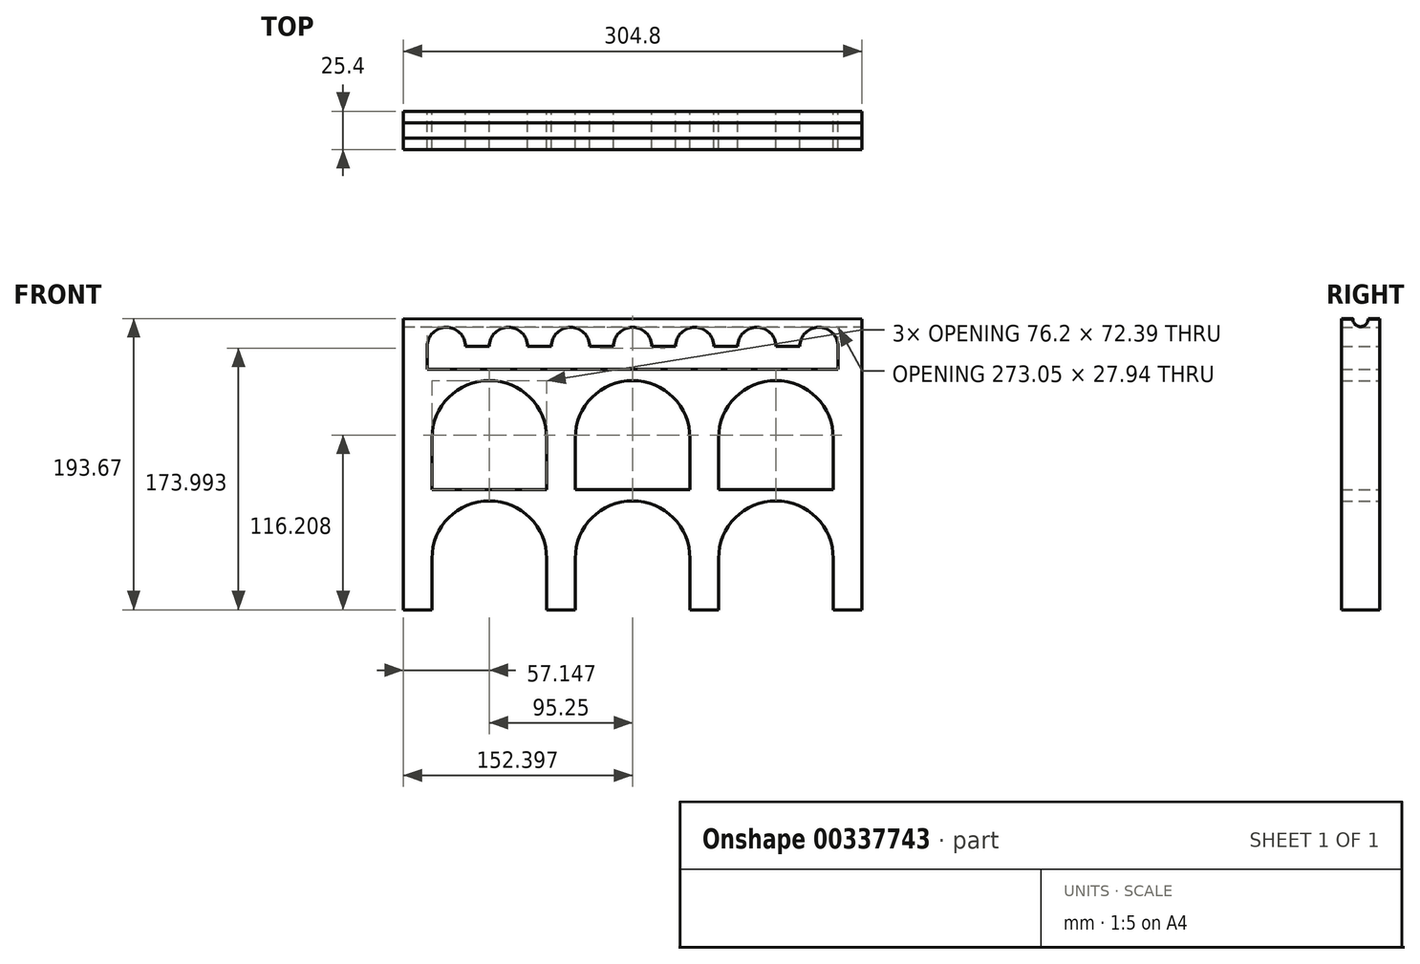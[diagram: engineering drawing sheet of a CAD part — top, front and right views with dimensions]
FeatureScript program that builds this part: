
annotation { "Feature Type Name" : "Feature", "Feature Type Description" : "" }
export const myFeature = defineFeature(function(context is Context, id is Id, definition is map)
    precondition{}
    {
        {
            var Q0;
            Q0=qCreatedBy(makeId("Front.planeOp"),FACE);
            var sketch = newSketch(context, id + "F0", { "sketchPlane" : qUnion([Q0])});
            skLineSegment(sketch, "E0.top", {"start": v(-1391.75, -516.72) * mm, "end": v(-1372.7, -516.72) * mm});
            skLineSegment(sketch, "E0.left", {"start": v(-1391.75, -482.43) * mm, "end": v(-1391.75, -516.72) * mm});
            skLineSegment(sketch, "E0.right", {"start": v(-1372.7, -482.43) * mm, "end": v(-1372.7, -516.72) * mm});
            skLineSegment(sketch, "E1.top", {"start": v(-1296.5, -516.72) * mm, "end": v(-1277.45, -516.72) * mm});
            skLineSegment(sketch, "E1.left", {"start": v(-1296.5, -482.43) * mm, "end": v(-1296.5, -516.72) * mm});
            skLineSegment(sketch, "E1.right", {"start": v(-1277.45, -482.43) * mm, "end": v(-1277.45, -516.72) * mm});
            skLineSegment(sketch, "E2.top", {"start": v(-1201.25, -516.72) * mm, "end": v(-1182.2, -516.72) * mm});
            skLineSegment(sketch, "E2.left", {"start": v(-1201.25, -482.43) * mm, "end": v(-1201.25, -516.72) * mm});
            skLineSegment(sketch, "E2.right", {"start": v(-1182.2, -482.43) * mm, "end": v(-1182.2, -516.72) * mm});
            skLineSegment(sketch, "E3.top", {"start": v(-1487, -516.72) * mm, "end": v(-1467.95, -516.72) * mm});
            skLineSegment(sketch, "E3.left", {"start": v(-1487, -482.43) * mm, "end": v(-1487, -516.72) * mm});
            skLineSegment(sketch, "E3.right", {"start": v(-1467.95, -482.43) * mm, "end": v(-1467.95, -516.72) * mm});
            skArc(sketch, "E4", {"start": v(-1391.75, -482.43) * mm, "mid": v(-1429.85, -444.33) * mm, "end": v(-1467.95, -482.43) * mm});
            skArc(sketch, "E5", {"start": v(-1296.5, -482.43) * mm, "mid": v(-1334.6, -444.33) * mm, "end": v(-1372.7, -482.43) * mm});
            skArc(sketch, "E6", {"start": v(-1201.25, -482.43) * mm, "mid": v(-1239.35, -444.33) * mm, "end": v(-1277.45, -482.43) * mm});
            skLineSegment(sketch, "E7", {"start": v(-1487, -482.43) * mm, "end": v(-1487, -436.7) * mm});
            skLineSegment(sketch, "E8", {"start": v(-1487, -436.7) * mm, "end": v(-1467.95, -436.7) * mm});
            skLineSegment(sketch, "E9", {"start": v(-1182.2, -482.43) * mm, "end": v(-1182.2, -436.7) * mm});
            skLineSegment(sketch, "E10.top", {"start": v(-1487, -402.42) * mm, "end": v(-1467.95, -402.42) * mm});
            skLineSegment(sketch, "E10.left", {"start": v(-1487, -436.7) * mm, "end": v(-1487, -402.42) * mm});
            skLineSegment(sketch, "E10.right", {"start": v(-1467.95, -436.7) * mm, "end": v(-1467.95, -402.42) * mm});
            skLineSegment(sketch, "E11.bottom", {"start": v(-1391.75, -436.7) * mm, "end": v(-1372.7, -436.7) * mm});
            skLineSegment(sketch, "E11.top", {"start": v(-1391.75, -402.42) * mm, "end": v(-1372.7, -402.42) * mm});
            skLineSegment(sketch, "E11.left", {"start": v(-1391.75, -436.7) * mm, "end": v(-1391.75, -402.42) * mm});
            skLineSegment(sketch, "E11.right", {"start": v(-1372.7, -436.7) * mm, "end": v(-1372.7, -402.42) * mm});
            skLineSegment(sketch, "E12.bottom", {"start": v(-1182.2, -436.7) * mm, "end": v(-1201.25, -436.7) * mm});
            skLineSegment(sketch, "E12.top", {"start": v(-1182.2, -402.42) * mm, "end": v(-1201.25, -402.42) * mm});
            skLineSegment(sketch, "E12.left", {"start": v(-1182.2, -436.7) * mm, "end": v(-1182.2, -402.42) * mm});
            skLineSegment(sketch, "E12.right", {"start": v(-1201.25, -436.7) * mm, "end": v(-1201.25, -402.42) * mm});
            skLineSegment(sketch, "E13.bottom", {"start": v(-1296.5, -436.7) * mm, "end": v(-1277.45, -436.7) * mm});
            skLineSegment(sketch, "E13.top", {"start": v(-1296.5, -402.42) * mm, "end": v(-1277.45, -402.42) * mm});
            skLineSegment(sketch, "E13.left", {"start": v(-1296.5, -436.7) * mm, "end": v(-1296.5, -402.42) * mm});
            skLineSegment(sketch, "E13.right", {"start": v(-1277.45, -436.7) * mm, "end": v(-1277.45, -402.42) * mm});
            skLineSegment(sketch, "E14.top", {"start": v(-1487, -356.7) * mm, "end": v(-1182.2, -356.7) * mm});
            skLineSegment(sketch, "E14.left", {"start": v(-1487, -402.42) * mm, "end": v(-1487, -356.7) * mm});
            skLineSegment(sketch, "E14.right", {"start": v(-1182.2, -402.42) * mm, "end": v(-1182.2, -356.7) * mm});
            skArc(sketch, "E15", {"start": v(-1391.75, -402.42) * mm, "mid": v(-1429.85, -364.32) * mm, "end": v(-1467.95, -402.42) * mm});
            skArc(sketch, "E16", {"start": v(-1296.5, -402.42) * mm, "mid": v(-1334.6, -364.32) * mm, "end": v(-1372.7, -402.42) * mm});
            skArc(sketch, "E17", {"start": v(-1201.25, -402.42) * mm, "mid": v(-1239.35, -364.32) * mm, "end": v(-1277.45, -402.42) * mm});
            skLineSegment(sketch, "E18.trimOffspring", {"start": v(-1201.25, -402.42) * mm, "end": v(-1182.2, -402.42) * mm});
            skLineSegment(sketch, "E19.trimOffspring", {"start": v(-1201.25, -436.7) * mm, "end": v(-1182.2, -436.7) * mm});
            skLineSegment(sketch, "E20", {"start": v(-1467.95, -436.7) * mm, "end": v(-1201.25, -436.7) * mm});
            skLineSegment(sketch, "E21.bottom", {"start": v(-1487, -356.7) * mm, "end": v(-1471.13, -356.7) * mm});
            skLineSegment(sketch, "E21.top", {"start": v(-1487, -341.46) * mm, "end": v(-1471.13, -341.46) * mm});
            skLineSegment(sketch, "E21.left", {"start": v(-1487, -356.7) * mm, "end": v(-1487, -341.46) * mm});
            skLineSegment(sketch, "E21.right", {"start": v(-1471.13, -356.7) * mm, "end": v(-1471.13, -341.46) * mm});
            skLineSegment(sketch, "E22.bottom", {"start": v(-1363.18, -356.7) * mm, "end": v(-1347.3, -356.7) * mm});
            skLineSegment(sketch, "E22.top", {"start": v(-1363.18, -341.46) * mm, "end": v(-1347.3, -341.46) * mm});
            skLineSegment(sketch, "E22.left", {"start": v(-1363.18, -356.7) * mm, "end": v(-1363.18, -341.46) * mm});
            skLineSegment(sketch, "E22.right", {"start": v(-1347.3, -356.7) * mm, "end": v(-1347.3, -341.46) * mm});
            skLineSegment(sketch, "E23.bottom", {"start": v(-1321.9, -356.7) * mm, "end": v(-1306.03, -356.7) * mm});
            skLineSegment(sketch, "E23.top", {"start": v(-1321.9, -341.46) * mm, "end": v(-1306.03, -341.46) * mm});
            skLineSegment(sketch, "E23.left", {"start": v(-1321.9, -356.7) * mm, "end": v(-1321.9, -341.46) * mm});
            skLineSegment(sketch, "E23.right", {"start": v(-1306.03, -356.7) * mm, "end": v(-1306.03, -341.46) * mm});
            skLineSegment(sketch, "E24.bottom", {"start": v(-1404.45, -356.7) * mm, "end": v(-1388.58, -356.7) * mm});
            skLineSegment(sketch, "E24.top", {"start": v(-1404.45, -341.46) * mm, "end": v(-1388.58, -341.46) * mm});
            skLineSegment(sketch, "E24.left", {"start": v(-1404.45, -356.7) * mm, "end": v(-1404.45, -341.46) * mm});
            skLineSegment(sketch, "E24.right", {"start": v(-1388.58, -356.7) * mm, "end": v(-1388.58, -341.46) * mm});
            skLineSegment(sketch, "E25.bottom", {"start": v(-1280.63, -356.7) * mm, "end": v(-1264.75, -356.7) * mm});
            skLineSegment(sketch, "E25.top", {"start": v(-1280.63, -341.46) * mm, "end": v(-1264.75, -341.46) * mm});
            skLineSegment(sketch, "E25.left", {"start": v(-1280.63, -356.7) * mm, "end": v(-1280.63, -341.46) * mm});
            skLineSegment(sketch, "E25.right", {"start": v(-1264.75, -356.7) * mm, "end": v(-1264.75, -341.46) * mm});
            skLineSegment(sketch, "E26.bottom", {"start": v(-1445.73, -356.7) * mm, "end": v(-1429.85, -356.7) * mm});
            skLineSegment(sketch, "E26.top", {"start": v(-1445.73, -341.46) * mm, "end": v(-1429.85, -341.46) * mm});
            skLineSegment(sketch, "E26.left", {"start": v(-1445.73, -356.7) * mm, "end": v(-1445.73, -341.46) * mm});
            skLineSegment(sketch, "E26.right", {"start": v(-1429.85, -356.7) * mm, "end": v(-1429.85, -341.46) * mm});
            skLineSegment(sketch, "E27.bottom", {"start": v(-1198.08, -356.7) * mm, "end": v(-1182.2, -356.7) * mm});
            skLineSegment(sketch, "E27.top", {"start": v(-1198.08, -341.46) * mm, "end": v(-1182.2, -341.46) * mm});
            skLineSegment(sketch, "E27.left", {"start": v(-1198.08, -356.7) * mm, "end": v(-1198.08, -341.46) * mm});
            skLineSegment(sketch, "E27.right", {"start": v(-1182.2, -356.7) * mm, "end": v(-1182.2, -341.46) * mm});
            skLineSegment(sketch, "E28.bottom", {"start": v(-1239.35, -356.7) * mm, "end": v(-1223.48, -356.7) * mm});
            skLineSegment(sketch, "E28.top", {"start": v(-1239.35, -341.46) * mm, "end": v(-1223.48, -341.46) * mm});
            skLineSegment(sketch, "E28.left", {"start": v(-1239.35, -356.7) * mm, "end": v(-1239.35, -341.46) * mm});
            skLineSegment(sketch, "E28.right", {"start": v(-1223.48, -356.7) * mm, "end": v(-1223.48, -341.46) * mm});
            skArc(sketch, "E29", {"start": v(-1445.73, -341.46) * mm, "mid": v(-1458.43, -328.76) * mm, "end": v(-1471.13, -341.46) * mm});
            skArc(sketch, "E30", {"start": v(-1404.45, -341.46) * mm, "mid": v(-1417.15, -328.76) * mm, "end": v(-1429.85, -341.46) * mm});
            skArc(sketch, "E31", {"start": v(-1363.18, -341.46) * mm, "mid": v(-1375.88, -328.76) * mm, "end": v(-1388.58, -341.46) * mm});
            skArc(sketch, "E32", {"start": v(-1321.9, -341.46) * mm, "mid": v(-1334.6, -328.76) * mm, "end": v(-1347.3, -341.46) * mm});
            skArc(sketch, "E33", {"start": v(-1280.63, -341.46) * mm, "mid": v(-1293.33, -328.76) * mm, "end": v(-1306.03, -341.46) * mm});
            skArc(sketch, "E34", {"start": v(-1239.35, -341.46) * mm, "mid": v(-1252.05, -328.76) * mm, "end": v(-1264.75, -341.46) * mm});
            skArc(sketch, "E35", {"start": v(-1198.08, -341.46) * mm, "mid": v(-1210.78, -328.76) * mm, "end": v(-1223.48, -341.46) * mm});
            skLineSegment(sketch, "E36", {"start": v(-1487, -341.46) * mm, "end": v(-1487, -323.05) * mm});
            skLineSegment(sketch, "E37", {"start": v(-1487, -323.05) * mm, "end": v(-1177.48, -323.32) * mm});
            skLineSegment(sketch, "E38", {"start": v(-1182.2, -341.46) * mm, "end": v(-1182.2, -323.31) * mm});
            skSolve(sketch);
        }
        {
            var Q0;
            Q0 = qSketchRegion(id + "F0", true);
            var Q1;
            {var subQ0=sQuery(id+"F0.wireOp",EDGE,"E11.left");Q1=makeQuery(id+"F0.imprint","IMPRINT",FACE,{"disambiguationData":[TD([[makeQuery(id+"F0.imprint","IMPRINT",EDGE,{"derivedFrom":subQ0}),-1.0]])]});}
            var Q2;
            {var subQ0=sQuery(id+"F0.wireOp",EDGE,"E13.left");Q2=makeQuery(id+"F0.imprint","IMPRINT",FACE,{"disambiguationData":[TD([[makeQuery(id+"F0.imprint","IMPRINT",EDGE,{"derivedFrom":subQ0}),-1.0]])]});}
            var Q3;
            Q3=makeQuery(id+"F0.imprint","IMPRINT",FACE,{"disambiguationData":[TD([[makeQuery(id+"F0.imprint","IMPRINT",EDGE,{"derivedFrom":sQuery(id+"F0.wireOp",EDGE,"E24.bottom")}),1.0]])]});
            var Q4;
            Q4=makeQuery(id+"F0.imprint","IMPRINT",FACE,{"disambiguationData":[TD([[makeQuery(id+"F0.imprint","IMPRINT",EDGE,{"derivedFrom":sQuery(id+"F0.wireOp",EDGE,"E22.bottom")}),1.0]])]});
            var Q5;
            Q5=makeQuery(id+"F0.imprint","IMPRINT",FACE,{"disambiguationData":[TD([[makeQuery(id+"F0.imprint","IMPRINT",EDGE,{"derivedFrom":sQuery(id+"F0.wireOp",EDGE,"E23.bottom")}),1.0]])]});
            var Q6;
            Q6=makeQuery(id+"F0.imprint","IMPRINT",FACE,{"disambiguationData":[TD([[makeQuery(id+"F0.imprint","IMPRINT",EDGE,{"derivedFrom":sQuery(id+"F0.wireOp",EDGE,"E25.bottom")}),1.0]])]});
            var Q7;
            Q7=makeQuery(id+"F0.imprint","IMPRINT",FACE,{"disambiguationData":[TD([[makeQuery(id+"F0.imprint","IMPRINT",EDGE,{"derivedFrom":sQuery(id+"F0.wireOp",EDGE,"E26.bottom")}),1.0]])]});
            var Q8;
            Q8=makeQuery(id+"F0.imprint","IMPRINT",FACE,{"disambiguationData":[TD([[makeQuery(id+"F0.imprint","IMPRINT",EDGE,{"derivedFrom":sQuery(id+"F0.wireOp",EDGE,"E28.bottom")}),1.0]])]});
            extrude(context, id + "F1", {"entities" : qUnion([Q0, Q1, Q2, Q3, Q4, Q5, Q6, Q7, Q8]), "depth" : 25.4 * mm});
        }
        {
            var Q0;
            Q0=makeQuery(id+"F1.opExtrude","SWEPT_FACE",FACE,{"disambiguationData":[OSD([sQuery(id+"F0.wireOp",EDGE,"E2.right"),sQuery(id+"F0.wireOp",EDGE,"E9"),sQuery(id+"F0.wireOp",EDGE,"E12.left"),sQuery(id+"F0.wireOp",EDGE,"E14.right"),sQuery(id+"F0.wireOp",EDGE,"E27.right"),sQuery(id+"F0.wireOp",EDGE,"E38")])]});
            var sketch = newSketch(context, id + "F2", { "sketchPlane" : qUnion([Q0])});
            skCircle(sketch, "E39", {"center": v(-12.7, -323.31) * mm, "radius": 5.08 * mm});
            skSolve(sketch);
        }
        {
            var Q0;
            Q0 = qSketchRegion(id + "F2", true);
            extrude(context, id + "F3", {"entities" : qUnion([Q0]), "operationType" : NewBodyOperationType.REMOVE, "endBound" : BoundingType.THROUGH_ALL, "oppositeDirection" : true, "depth" : 25.4 * mm});
        }
    });
